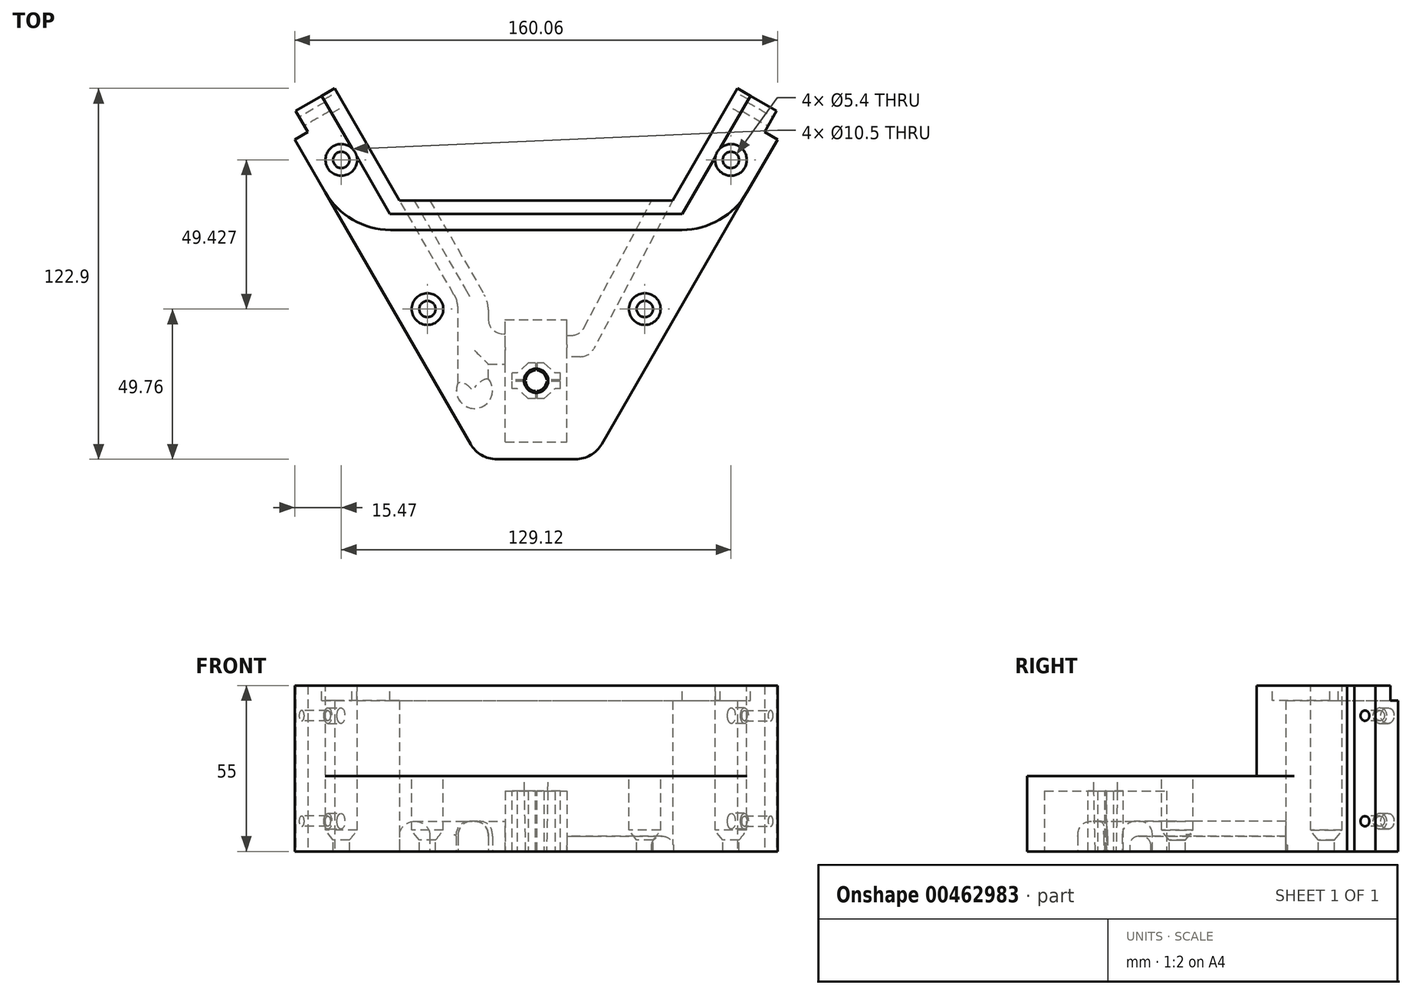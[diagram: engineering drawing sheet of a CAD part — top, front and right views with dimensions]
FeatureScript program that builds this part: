
annotation { "Feature Type Name" : "Feature", "Feature Type Description" : "" }
export const myFeature = defineFeature(function(context is Context, id is Id, definition is map)
    precondition{}
    {
        {
            var Q0;
            Q0=qCreatedBy(makeId("Top.planeOp"),FACE);
            var sketch = newSketch(context, id + "F0", { "sketchPlane" : qUnion([Q0])});
            skLineSegment(sketch, "E0.bottom", {"start": v(53.2, 49.76) * mm, "end": v(-53.2, 49.76) * mm, "construction": true});
            skLineSegment(sketch, "E0.top", {"start": v(53.2, -49.76) * mm, "end": v(-53.2, -49.76) * mm, "construction": true});
            skLineSegment(sketch, "E0.left", {"start": v(53.2, 49.76) * mm, "end": v(53.2, -49.76) * mm, "construction": true});
            skLineSegment(sketch, "E0.right", {"start": v(-53.2, 49.76) * mm, "end": v(-53.2, -49.76) * mm, "construction": true});
            skPoint(sketch, "E0.middle", {"position": v(0, 0) * mm});
            skLineSegment(sketch, "E1", {"start": v(-53.2, 49.76) * mm, "end": v(-48, 52.76) * mm, "construction": true});
            skLineSegment(sketch, "E2", {"start": v(-48, 52.76) * mm, "end": v(-40.64, 40) * mm, "construction": true});
            skLineSegment(sketch, "E3", {"start": v(53.2, 49.76) * mm, "end": v(48, 52.76) * mm, "construction": true});
            skLineSegment(sketch, "E4", {"start": v(48, 52.76) * mm, "end": v(40.64, 40) * mm, "construction": true});
            skLineSegment(sketch, "E5", {"start": v(16.54, -13.75) * mm, "end": v(33.86, -23.75) * mm, "construction": true});
            skLineSegment(sketch, "E6", {"start": v(80.03, 56.21) * mm, "end": v(21.73, -44.76) * mm});
            skLineSegment(sketch, "E7", {"start": v(-16.53, -13.75) * mm, "end": v(-33.86, -23.75) * mm, "construction": true});
            skLineSegment(sketch, "E8", {"start": v(-80.03, 56.21) * mm, "end": v(-21.73, -44.76) * mm});
            skLineSegment(sketch, "E9", {"start": v(-13.07, -49.76) * mm, "end": v(13.07, -49.76) * mm});
            skPoint(sketch, "E10.visualSharp", {"position": v(-18.84, -49.76) * mm});
            skArc(sketch, "E10.filletArc", {"start": v(-21.73, -44.76) * mm, "mid": v(-18.07, -48.42) * mm, "end": v(-13.07, -49.76) * mm});
            skPoint(sketch, "E11.visualSharp", {"position": v(18.84, -49.76) * mm});
            skArc(sketch, "E11.filletArc", {"start": v(13.07, -49.76) * mm, "mid": v(18.07, -48.42) * mm, "end": v(21.73, -44.76) * mm});
            skLineSegment(sketch, "E12.bottom", {"start": v(10, -43.76) * mm, "end": v(-10, -43.76) * mm, "construction": true});
            skLineSegment(sketch, "E12.top", {"start": v(10, -3.76) * mm, "end": v(-10, -3.76) * mm, "construction": true});
            skLineSegment(sketch, "E12.left", {"start": v(10, -43.76) * mm, "end": v(10, -3.76) * mm, "construction": true});
            skLineSegment(sketch, "E12.right", {"start": v(-10, -43.76) * mm, "end": v(-10, -3.76) * mm, "construction": true});
            skPoint(sketch, "E12.middle", {"position": v(0, -23.76) * mm});
            skLineSegment(sketch, "E13", {"start": v(14.22, 4.24) * mm, "end": v(-14.22, 4.24) * mm, "construction": true});
            skPoint(sketch, "E14.orphan", {"position": v(-19.1, 2.67) * mm});
            skPoint(sketch, "E15.orphan", {"position": v(19.1, 2.67) * mm});
            skPoint(sketch, "E16.visualSharp", {"position": v(-20, 4.24) * mm});
            skArc(sketch, "E16.filletArc", {"start": v(-22.88, 9.24) * mm, "mid": v(-19.22, 5.58) * mm, "end": v(-14.22, 4.24) * mm, "construction": true});
            skPoint(sketch, "E17.visualSharp", {"position": v(20, 4.24) * mm});
            skArc(sketch, "E17.filletArc", {"start": v(14.22, 4.24) * mm, "mid": v(19.22, 5.58) * mm, "end": v(22.88, 9.24) * mm, "construction": true});
            skLineSegment(sketch, "E18", {"start": v(32.55, 32) * mm, "end": v(-32.55, 31.99) * mm, "construction": true});
            skLineSegment(sketch, "E19", {"start": v(-45.25, 35.99) * mm, "end": v(45.25, 36) * mm});
            skLineSegment(sketch, "E20.trimOffspring", {"start": v(-34.29, 29) * mm, "end": v(-22.88, 9.24) * mm, "construction": true});
            skLineSegment(sketch, "E21.trimOffspring", {"start": v(34.29, 29) * mm, "end": v(22.88, 9.24) * mm, "construction": true});
            skPoint(sketch, "E22.visualSharp", {"position": v(-36.02, 31.99) * mm});
            skArc(sketch, "E22.filletArc", {"start": v(-32.55, 31.99) * mm, "mid": v(-34.29, 30.99) * mm, "end": v(-34.29, 28.99) * mm, "construction": true});
            skPoint(sketch, "E23.visualSharp", {"position": v(36.02, 32) * mm});
            skArc(sketch, "E23.filletArc", {"start": v(34.29, 29) * mm, "mid": v(34.29, 31) * mm, "end": v(32.55, 32) * mm, "construction": true});
            skPoint(sketch, "E24.visualSharp", {"position": v(-38.33, 36) * mm});
            skArc(sketch, "E24.filletArc", {"start": v(-40.64, 39.99) * mm, "mid": v(-37.7, 37.06) * mm, "end": v(-33.7, 36) * mm, "construction": true});
            skPoint(sketch, "E25.visualSharp", {"position": v(38.33, 36) * mm});
            skArc(sketch, "E25.filletArc", {"start": v(33.7, 36) * mm, "mid": v(37.7, 37.06) * mm, "end": v(40.64, 40) * mm, "construction": true});
            skLineSegment(sketch, "E26", {"start": v(-53.2, 29.76) * mm, "end": v(-15.63, -35.33) * mm, "construction": true});
            skLineSegment(sketch, "E27", {"start": v(53.2, 29.76) * mm, "end": v(15.63, -35.33) * mm, "construction": true});
            skCircle(sketch, "E28", {"center": v(-20.45, -26.98) * mm, "radius": 6 * mm, "construction": true});
            skCircle(sketch, "E29", {"center": v(20.45, -26.98) * mm, "radius": 6 * mm, "construction": true});
            skLineSegment(sketch, "E30", {"start": v(-45.25, 35.99) * mm, "end": v(-66.7, 73.14) * mm});
            skLineSegment(sketch, "E31", {"start": v(-66.7, 73.14) * mm, "end": v(-79.7, 65.64) * mm});
            skLineSegment(sketch, "E32", {"start": v(45.25, 36) * mm, "end": v(66.7, 73.14) * mm});
            skLineSegment(sketch, "E33", {"start": v(66.7, 73.14) * mm, "end": v(79.7, 65.64) * mm});
            skLineSegment(sketch, "E34", {"start": v(-45.25, 35.99) * mm, "end": v(-16.53, -13.75) * mm, "construction": true});
            skLineSegment(sketch, "E35", {"start": v(45.25, 36) * mm, "end": v(45.25, 36) * mm});
            skLineSegment(sketch, "E36", {"start": v(45.25, 36) * mm, "end": v(16.54, -13.75) * mm, "construction": true});
            skLineSegment(sketch, "E37", {"start": v(-79.7, 65.64) * mm, "end": v(-75.7, 58.71) * mm});
            skLineSegment(sketch, "E38", {"start": v(-75.7, 58.71) * mm, "end": v(-80.03, 56.21) * mm});
            skLineSegment(sketch, "E39", {"start": v(79.7, 65.64) * mm, "end": v(75.7, 58.71) * mm});
            skLineSegment(sketch, "E40", {"start": v(75.7, 58.71) * mm, "end": v(80.03, 56.21) * mm});
            skSolve(sketch);
        }
        {
            var Q0;
            Q0 = qSketchRegion(id + "F0", true);
            extrude(context, id + "F1", {"entities" : qUnion([Q0]), "depth" : 25 * mm, "offsetDistance" : 25 * mm});
        }
        {
            var Q0;
            Q0=makeQuery(id+"F0.imprint","IMPRINT",FACE,{"disambiguationData":[TD([[makeQuery(id+"F0.imprint","IMPRINT",EDGE,{"derivedFrom":sQuery(id+"F0.wireOp",EDGE,"E6")}),-1.0]])]});
            var sketch = newSketch(context, id + "F2", { "sketchPlane" : qUnion([Q0])});
            skLineSegment(sketch, "E41.bottom", {"start": v(10, -43.74) * mm, "end": v(-10, -43.74) * mm});
            skLineSegment(sketch, "E41.top", {"start": v(10, -3.74) * mm, "end": v(-10, -3.74) * mm});
            skLineSegment(sketch, "E41.left", {"start": v(10, -43.74) * mm, "end": v(10, -3.74) * mm});
            skLineSegment(sketch, "E41.right", {"start": v(-10, -43.74) * mm, "end": v(-10, -18.24) * mm});
            skPoint(sketch, "E41.middle", {"position": v(0, -23.74) * mm});
            skArc(sketch, "E42", {"start": v(-25.87, -24.4) * mm, "mid": v(-19.66, -32.9) * mm, "end": v(-15.87, -23.08) * mm});
            skLineSegment(sketch, "E43", {"start": v(-25.87, -24.4) * mm, "end": v(-25.87, -0.24) * mm});
            skLineSegment(sketch, "E44", {"start": v(-27.21, 4.76) * mm, "end": v(-45.25, 36) * mm});
            skLineSegment(sketch, "E45", {"start": v(-45.25, 36) * mm, "end": v(-35.25, 36) * mm});
            skLineSegment(sketch, "E46", {"start": v(-35.25, 36) * mm, "end": v(-17.21, 4.76) * mm});
            skPoint(sketch, "E47.visualSharp", {"position": v(-25.87, 2.44) * mm});
            skArc(sketch, "E47.filletArc", {"start": v(-25.87, -0.24) * mm, "mid": v(-26.21, 2.35) * mm, "end": v(-27.21, 4.76) * mm});
            skPoint(sketch, "E48.visualSharp", {"position": v(-15.87, 2.44) * mm});
            skArc(sketch, "E48.filletArc", {"start": v(-15.87, -0.24) * mm, "mid": v(-16.21, 2.35) * mm, "end": v(-17.21, 4.76) * mm});
            skLineSegment(sketch, "E49", {"start": v(-15.87, -23.08) * mm, "end": v(-15.87, -18.24) * mm});
            skLineSegment(sketch, "E50", {"start": v(-15.87, -18.24) * mm, "end": v(-10, -18.24) * mm});
            skLineSegment(sketch, "E51", {"start": v(-10.87, -8.24) * mm, "end": v(-10, -8.24) * mm});
            skLineSegment(sketch, "E52", {"start": v(-15.87, -0.24) * mm, "end": v(-15.87, -3.24) * mm});
            skPoint(sketch, "E53.visualSharp", {"position": v(-15.87, -8.24) * mm});
            skArc(sketch, "E53.filletArc", {"start": v(-15.87, -3.24) * mm, "mid": v(-14.4, -6.77) * mm, "end": v(-10.87, -8.24) * mm});
            skLineSegment(sketch, "E54.trimOffspring", {"start": v(-10, -8.24) * mm, "end": v(-10, -3.74) * mm});
            skSolve(sketch);
        }
        {
            var Q0;
            Q0 = qSketchRegion(id + "F2", true);
            extrude(context, id + "F3", {"entities" : qUnion([Q0]), "operationType" : NewBodyOperationType.REMOVE, "depth" : 10 * mm, "offsetDistance" : 25 * mm});
        }
        {
            var Q0;
            Q0=makeQuery(id+"F3.boolean.opBoolean","COPY",EDGE,{"derivedFrom":makeQuery(id+"F3.opExtrude","CAP_EDGE",EDGE,{"disambiguationData":[OSD([sQuery(id+"F2.wireOp",EDGE,"E44")])],"isStart":false})});
            var Q1;
            Q1=makeQuery(id+"F3.boolean.opBoolean","COPY",EDGE,{"derivedFrom":makeQuery(id+"F3.opExtrude","CAP_EDGE",EDGE,{"disambiguationData":[OSD([sQuery(id+"F2.wireOp",EDGE,"E46")])],"isStart":false})});
            var Q2;
            Q2=makeQuery(id+"F3.boolean.opBoolean","COPY",EDGE,{"derivedFrom":makeQuery(id+"F3.opExtrude","CAP_EDGE",EDGE,{"disambiguationData":[OSD([sQuery(id+"F2.wireOp",EDGE,"E50")])],"isStart":false})});
            var Q3;
            Q3=makeQuery(id+"F3.boolean.opBoolean","COPY",EDGE,{"derivedFrom":makeQuery(id+"F3.opExtrude","CAP_EDGE",EDGE,{"disambiguationData":[OSD([sQuery(id+"F2.wireOp",EDGE,"E49")])],"isStart":false})});
            fillet(context, id + "F4", {"entities" : qUnion([Q0, Q1, Q2, Q3]), "radius" : 4.5 * mm, "tangentPropagation" : true, "allowEdgeOverflow" : false});
        }
        {
            var Q0;
            Q0=makeQuery(id+"F3.boolean.opBoolean","COPY",EDGE,{"derivedFrom":makeQuery(id+"F3.opExtrude","CAP_EDGE",EDGE,{"disambiguationData":[OSD([sQuery(id+"F2.wireOp",EDGE,"E42")])],"isStart":false})});
            fillet(context, id + "F5", {"entities" : qUnion([Q0]), "radius" : 5 * mm, "rho" : 0.5, "crossSection" : FilletCrossSection.CONIC, "allowEdgeOverflow" : false});
        }
        {
            var Q0;
            Q0=makeQuery(id+"F0.imprint","IMPRINT",FACE,{"disambiguationData":[TD([[makeQuery(id+"F0.imprint","IMPRINT",EDGE,{"derivedFrom":sQuery(id+"F0.wireOp",EDGE,"E6")}),-1.0]])]});
            var sketch = newSketch(context, id + "F6", { "sketchPlane" : qUnion([Q0])});
            skLineSegment(sketch, "E55", {"start": v(9.52, -8.78) * mm, "end": v(11.51, -8.78) * mm});
            skLineSegment(sketch, "E56", {"start": v(15.93, -6.12) * mm, "end": v(39.82, 38.9) * mm});
            skLineSegment(sketch, "E57", {"start": v(39.82, 38.9) * mm, "end": v(46.82, 38.9) * mm});
            skLineSegment(sketch, "E58", {"start": v(46.82, 38.9) * mm, "end": v(19.1, -13.15) * mm});
            skLineSegment(sketch, "E59", {"start": v(14.7, -15.8) * mm, "end": v(9.5, -15.8) * mm});
            skLineSegment(sketch, "E60", {"start": v(9.5, -15.8) * mm, "end": v(9.52, -8.78) * mm});
            skPoint(sketch, "E61.visualSharp", {"position": v(14.52, -8.78) * mm});
            skArc(sketch, "E61.filletArc", {"start": v(11.51, -8.78) * mm, "mid": v(14.09, -8.06) * mm, "end": v(15.93, -6.12) * mm});
            skPoint(sketch, "E62.visualSharp", {"position": v(17.7, -15.8) * mm});
            skArc(sketch, "E62.filletArc", {"start": v(14.7, -15.8) * mm, "mid": v(17.27, -15.09) * mm, "end": v(19.1, -13.15) * mm});
            skSolve(sketch);
        }
        {
            var Q0;
            Q0 = qSketchRegion(id + "F6", true);
            extrude(context, id + "F7", {"entities" : qUnion([Q0]), "operationType" : NewBodyOperationType.REMOVE, "depth" : 5 * mm, "offsetDistance" : 25 * mm});
        }
        {
            var Q0;
            Q0=makeQuery(id+"F7.boolean.opBoolean","COPY",EDGE,{"derivedFrom":makeQuery(id+"F7.opExtrude","CAP_EDGE",EDGE,{"disambiguationData":[OSD([sQuery(id+"F6.wireOp",EDGE,"E58")])],"isStart":false})});
            var Q1;
            Q1=makeQuery(id+"F7.boolean.opBoolean","COPY",EDGE,{"derivedFrom":makeQuery(id+"F7.opExtrude","CAP_EDGE",EDGE,{"disambiguationData":[OSD([sQuery(id+"F6.wireOp",EDGE,"E56")])],"isStart":false})});
            fillet(context, id + "F8", {"entities" : qUnion([Q0, Q1]), "radius" : 3 * mm, "tangentPropagation" : true, "allowEdgeOverflow" : false});
        }
        {
            var Q0;
            Q0=makeQuery(id+"F0.imprint","IMPRINT",FACE,{"disambiguationData":[TD([[makeQuery(id+"F0.imprint","IMPRINT",EDGE,{"derivedFrom":sQuery(id+"F0.wireOp",EDGE,"E6")}),-1.0]])]});
            var sketch = newSketch(context, id + "F9", { "sketchPlane" : qUnion([Q0])});
            skLineSegment(sketch, "E63.bottom", {"start": v(-10.25, -44) * mm, "end": v(10.25, -44) * mm});
            skLineSegment(sketch, "E63.top", {"start": v(-10.25, -3.5) * mm, "end": v(10.25, -3.5) * mm});
            skLineSegment(sketch, "E63.left", {"start": v(-10.25, -44) * mm, "end": v(-10.25, -3.5) * mm});
            skLineSegment(sketch, "E63.right", {"start": v(10.25, -44) * mm, "end": v(10.25, -3.5) * mm});
            skSolve(sketch);
        }
        {
            var Q0;
            Q0 = qSketchRegion(id + "F9", true);
            extrude(context, id + "F10", {"entities" : qUnion([Q0]), "operationType" : NewBodyOperationType.REMOVE, "depth" : 20 * mm, "offsetDistance" : 25 * mm});
        }
        {
            var Q0;
            Q0=makeQuery(id+"F0.imprint","IMPRINT",FACE,{"disambiguationData":[TD([[makeQuery(id+"F0.imprint","IMPRINT",EDGE,{"derivedFrom":sQuery(id+"F0.wireOp",EDGE,"E6")}),-1.0]])]});
            var sketch = newSketch(context, id + "F11", { "sketchPlane" : qUnion([Q0])});
            skLineSegment(sketch, "E64.bottom", {"start": v(2.6, -17.89) * mm, "end": v(-2.6, -17.89) * mm, "construction": true});
            skLineSegment(sketch, "E64.top", {"start": v(2.6, -29.64) * mm, "end": v(-2.6, -29.64) * mm, "construction": true});
            skLineSegment(sketch, "E64.left", {"start": v(8, -21.16) * mm, "end": v(8, -26.36) * mm, "construction": true});
            skLineSegment(sketch, "E64.right", {"start": v(-8, -21.16) * mm, "end": v(-8, -26.36) * mm, "construction": true});
            skPoint(sketch, "E64.middle", {"position": v(0, -23.76) * mm});
            skLineSegment(sketch, "E65.bottom", {"start": v(8, -26.36) * mm, "end": v(6.25, -26.36) * mm});
            skLineSegment(sketch, "E65.top", {"start": v(8, -21.16) * mm, "end": v(6.25, -21.16) * mm});
            skLineSegment(sketch, "E65.left", {"start": v(8, -26.36) * mm, "end": v(8, -21.16) * mm});
            skLineSegment(sketch, "E65.right", {"start": v(-8, -26.36) * mm, "end": v(-8, -21.16) * mm});
            skLineSegment(sketch, "E66.bottom", {"start": v(2.6, -29.64) * mm, "end": v(-2.6, -29.64) * mm});
            skLineSegment(sketch, "E66.top", {"start": v(2.6, -17.89) * mm, "end": v(-2.6, -17.89) * mm});
            skLineSegment(sketch, "E66.left", {"start": v(2.6, -29.64) * mm, "end": v(2.6, -17.89) * mm, "construction": true});
            skLineSegment(sketch, "E66.right", {"start": v(-2.6, -29.64) * mm, "end": v(-2.6, -17.89) * mm, "construction": true});
            skPoint(sketch, "E67.orphan", {"position": v(-8, -17.89) * mm});
            skPoint(sketch, "E68.orphan", {"position": v(-8, -29.64) * mm});
            skPoint(sketch, "E69.orphan", {"position": v(8, -29.64) * mm});
            skPoint(sketch, "E70.orphan", {"position": v(8, -17.89) * mm});
            skLineSegment(sketch, "E71", {"start": v(-6.25, -26.36) * mm, "end": v(-6.25, -21.16) * mm, "construction": true});
            skLineSegment(sketch, "E72", {"start": v(6.25, -26.36) * mm, "end": v(6.25, -21.16) * mm, "construction": true});
            skLineSegment(sketch, "E73", {"start": v(-2.6, -29.64) * mm, "end": v(-6.25, -26.36) * mm});
            skLineSegment(sketch, "E74", {"start": v(2.6, -29.64) * mm, "end": v(6.25, -26.36) * mm});
            skLineSegment(sketch, "E75", {"start": v(2.6, -17.89) * mm, "end": v(6.25, -21.16) * mm});
            skLineSegment(sketch, "E76", {"start": v(-2.6, -17.89) * mm, "end": v(-6.25, -21.16) * mm});
            skLineSegment(sketch, "E77", {"start": v(-6.25, -26.36) * mm, "end": v(-8, -26.36) * mm});
            skLineSegment(sketch, "E78", {"start": v(6.25, -26.36) * mm, "end": v(-6.25, -26.36) * mm, "construction": true});
            skLineSegment(sketch, "E79", {"start": v(6.25, -21.16) * mm, "end": v(-6.25, -21.16) * mm, "construction": true});
            skLineSegment(sketch, "E80", {"start": v(-6.25, -21.16) * mm, "end": v(-8, -21.16) * mm});
            skSolve(sketch);
        }
        {
            var Q0;
            Q0 = qSketchRegion(id + "F11", true);
            extrude(context, id + "F12", {"entities" : qUnion([Q0]), "operationType" : NewBodyOperationType.ADD, "depth" : 20 * mm, "offsetDistance" : 25 * mm});
        }
        {
            var Q0;
            Q0=makeQuery(id+"F1.opExtrude","CAP_FACE",FACE,{"disambiguationData":[OSD([sQuery(id+"F0.wireOp",EDGE,"E6"),sQuery(id+"F0.wireOp",EDGE,"E8"),sQuery(id+"F0.wireOp",EDGE,"E9"),sQuery(id+"F0.wireOp",EDGE,"E10.filletArc"),sQuery(id+"F0.wireOp",EDGE,"E11.filletArc"),sQuery(id+"F0.wireOp",EDGE,"E19"),sQuery(id+"F0.wireOp",EDGE,"E30"),sQuery(id+"F0.wireOp",EDGE,"E31"),sQuery(id+"F0.wireOp",EDGE,"E32"),sQuery(id+"F0.wireOp",EDGE,"E33")])],"isStart":false});
            var sketch = newSketch(context, id + "F13", { "sketchPlane" : qUnion([Q0])});
            skCircle(sketch, "E81", {"center": v(0, -23.76) * mm, "radius": 4 * mm});
            skSolve(sketch);
        }
        {
            var Q0;
            Q0 = qSketchRegion(id + "F13", true);
            extrude(context, id + "F14", {"entities" : qUnion([Q0]), "operationType" : NewBodyOperationType.REMOVE, "oppositeDirection" : true, "depth" : 25 * mm, "offsetDistance" : 25 * mm, "hasDraft" : true, "draftAngle" : 1.25 * degree, "draftPullDirection" : true});
        }
        {
            var Q0;
            Q0=makeQuery(id+"F0.imprint","IMPRINT",FACE,{"disambiguationData":[TD([[makeQuery(id+"F0.imprint","IMPRINT",EDGE,{"derivedFrom":sQuery(id+"F0.wireOp",EDGE,"E6")}),-1.0]])]});
            var sketch = newSketch(context, id + "F15", { "sketchPlane" : qUnion([Q0])});
            skLineSegment(sketch, "E82.bottom", {"start": v(8.1, -23.51) * mm, "end": v(0.25, -23.51) * mm});
            skLineSegment(sketch, "E82.top", {"start": v(8.1, -24.01) * mm, "end": v(0.25, -24.01) * mm});
            skLineSegment(sketch, "E82.left", {"start": v(8.1, -23.51) * mm, "end": v(8.1, -24.01) * mm});
            skLineSegment(sketch, "E82.right", {"start": v(-8.1, -23.51) * mm, "end": v(-8.1, -24.01) * mm});
            skPoint(sketch, "E82.middle", {"position": v(0, -23.76) * mm});
            skLineSegment(sketch, "E83.bottom", {"start": v(0.25, -17.76) * mm, "end": v(-0.25, -17.76) * mm});
            skLineSegment(sketch, "E83.top", {"start": v(0.25, -29.76) * mm, "end": v(-0.25, -29.76) * mm});
            skLineSegment(sketch, "E83.left", {"start": v(0.25, -17.76) * mm, "end": v(0.25, -23.51) * mm});
            skLineSegment(sketch, "E83.right", {"start": v(-0.25, -17.76) * mm, "end": v(-0.25, -23.51) * mm});
            skLineSegment(sketch, "E84.trimOffspring", {"start": v(-0.25, -24.01) * mm, "end": v(-0.25, -29.76) * mm});
            skLineSegment(sketch, "E85.trimOffspring", {"start": v(-0.25, -24.01) * mm, "end": v(-8.1, -24.01) * mm});
            skLineSegment(sketch, "E86.trimOffspring", {"start": v(0.25, -24.01) * mm, "end": v(0.25, -29.76) * mm});
            skLineSegment(sketch, "E87.trimOffspring", {"start": v(-0.25, -23.51) * mm, "end": v(-8.1, -23.51) * mm});
            skSolve(sketch);
        }
        {
            var Q0;
            Q0 = qSketchRegion(id + "F15", true);
            extrude(context, id + "F16", {"entities" : qUnion([Q0]), "operationType" : NewBodyOperationType.REMOVE, "depth" : 20 * mm, "offsetDistance" : 25 * mm});
        }
        {
            var Q0;
            Q0=makeQuery(id+"F1.opExtrude","CAP_FACE",FACE,{"disambiguationData":[OSD([sQuery(id+"F0.wireOp",EDGE,"E6"),sQuery(id+"F0.wireOp",EDGE,"E8"),sQuery(id+"F0.wireOp",EDGE,"E9"),sQuery(id+"F0.wireOp",EDGE,"E10.filletArc"),sQuery(id+"F0.wireOp",EDGE,"E11.filletArc"),sQuery(id+"F0.wireOp",EDGE,"E19"),sQuery(id+"F0.wireOp",EDGE,"E30"),sQuery(id+"F0.wireOp",EDGE,"E31"),sQuery(id+"F0.wireOp",EDGE,"E32"),sQuery(id+"F0.wireOp",EDGE,"E33")])],"isStart":false});
            var sketch = newSketch(context, id + "F17", { "sketchPlane" : qUnion([Q0])});
            skLineSegment(sketch, "E88", {"start": v(-45.25, 35.99) * mm, "end": v(-66.7, 73.14) * mm});
            skLineSegment(sketch, "E89", {"start": v(-66.7, 73.14) * mm, "end": v(-79.7, 65.64) * mm});
            skLineSegment(sketch, "E90", {"start": v(-80.03, 56.21) * mm, "end": v(-69.94, 38.74) * mm});
            skLineSegment(sketch, "E91", {"start": v(-48.29, 26.24) * mm, "end": v(48.29, 26.24) * mm});
            skLineSegment(sketch, "E92", {"start": v(69.94, 38.74) * mm, "end": v(80.03, 56.21) * mm});
            skLineSegment(sketch, "E93", {"start": v(79.7, 65.64) * mm, "end": v(66.7, 73.14) * mm});
            skLineSegment(sketch, "E94", {"start": v(66.7, 73.14) * mm, "end": v(45.25, 36) * mm});
            skLineSegment(sketch, "E95", {"start": v(45.25, 36) * mm, "end": v(-45.25, 35.99) * mm});
            skPoint(sketch, "E96.visualSharp", {"position": v(-62.72, 26.24) * mm});
            skArc(sketch, "E96.filletArc", {"start": v(-69.94, 38.74) * mm, "mid": v(-60.79, 29.59) * mm, "end": v(-48.29, 26.24) * mm});
            skPoint(sketch, "E97.visualSharp", {"position": v(62.72, 26.24) * mm});
            skArc(sketch, "E97.filletArc", {"start": v(48.29, 26.24) * mm, "mid": v(60.79, 29.59) * mm, "end": v(69.94, 38.74) * mm});
            skLineSegment(sketch, "E98", {"start": v(-79.7, 65.64) * mm, "end": v(-75.7, 58.71) * mm});
            skLineSegment(sketch, "E99", {"start": v(-75.7, 58.71) * mm, "end": v(-80.03, 56.21) * mm});
            skLineSegment(sketch, "E100", {"start": v(79.7, 65.64) * mm, "end": v(75.7, 58.71) * mm});
            skLineSegment(sketch, "E101", {"start": v(75.7, 58.71) * mm, "end": v(80.03, 56.21) * mm});
            skSolve(sketch);
        }
        {
            var Q0;
            Q0 = qSketchRegion(id + "F17", true);
            extrude(context, id + "F18", {"entities" : qUnion([Q0]), "operationType" : NewBodyOperationType.ADD, "depth" : 30 * mm, "offsetDistance" : 25 * mm});
        }
        {
            var Q0;
            Q0=makeQuery(id+"F18.opExtrude","CAP_FACE",FACE,{"disambiguationData":[OSD([sQuery(id+"F17.wireOp",EDGE,"E88"),sQuery(id+"F17.wireOp",EDGE,"E89"),sQuery(id+"F17.wireOp",EDGE,"E90"),sQuery(id+"F17.wireOp",EDGE,"E91"),sQuery(id+"F17.wireOp",EDGE,"E92"),sQuery(id+"F17.wireOp",EDGE,"E93"),sQuery(id+"F17.wireOp",EDGE,"E94"),sQuery(id+"F17.wireOp",EDGE,"E95"),sQuery(id+"F17.wireOp",EDGE,"E96.filletArc"),sQuery(id+"F17.wireOp",EDGE,"E97.filletArc")])],"isStart":false});
            var sketch = newSketch(context, id + "F19", { "sketchPlane" : qUnion([Q0])});
            skLineSegment(sketch, "E102", {"start": v(-45.25, 35.99) * mm, "end": v(-66.7, 73.14) * mm});
            skLineSegment(sketch, "E103", {"start": v(-66.7, 73.14) * mm, "end": v(-71.04, 70.64) * mm});
            skLineSegment(sketch, "E104", {"start": v(-71.04, 70.64) * mm, "end": v(-48.44, 31.5) * mm});
            skLineSegment(sketch, "E105", {"start": v(-48.44, 31.5) * mm, "end": v(48.44, 31.5) * mm});
            skLineSegment(sketch, "E106", {"start": v(48.44, 31.5) * mm, "end": v(71.04, 70.64) * mm});
            skLineSegment(sketch, "E107", {"start": v(71.04, 70.64) * mm, "end": v(66.7, 73.14) * mm});
            skLineSegment(sketch, "E108", {"start": v(66.7, 73.14) * mm, "end": v(45.25, 36) * mm});
            skLineSegment(sketch, "E109", {"start": v(45.25, 36) * mm, "end": v(-45.25, 35.99) * mm});
            skSolve(sketch);
        }
        {
            var Q0;
            Q0 = qSketchRegion(id + "F19", true);
            extrude(context, id + "F20", {"entities" : qUnion([Q0]), "operationType" : NewBodyOperationType.REMOVE, "oppositeDirection" : true, "depth" : 5 * mm, "offsetDistance" : 25 * mm});
        }
        {
            var Q0;
            Q0=makeQuery(id+"F18.opExtrude","CAP_FACE",FACE,{"disambiguationData":[OSD([sQuery(id+"F17.wireOp",EDGE,"E88"),sQuery(id+"F17.wireOp",EDGE,"E89"),sQuery(id+"F17.wireOp",EDGE,"E90"),sQuery(id+"F17.wireOp",EDGE,"E91"),sQuery(id+"F17.wireOp",EDGE,"E92"),sQuery(id+"F17.wireOp",EDGE,"E93"),sQuery(id+"F17.wireOp",EDGE,"E94"),sQuery(id+"F17.wireOp",EDGE,"E95"),sQuery(id+"F17.wireOp",EDGE,"E96.filletArc"),sQuery(id+"F17.wireOp",EDGE,"E97.filletArc")])],"isStart":false});
            var sketch = newSketch(context, id + "F21", { "sketchPlane" : qUnion([Q0])});
            skLineSegment(sketch, "E110", {"start": v(-75.37, 68.14) * mm, "end": v(-53.4, 30.1) * mm, "construction": true});
            skLineSegment(sketch, "E111", {"start": v(75.37, 68.14) * mm, "end": v(55.87, 34.37) * mm, "construction": true});
            skLineSegment(sketch, "E112", {"start": v(-89.25, 49.43) * mm, "end": v(82.56, 49.43) * mm, "construction": true});
            skCircle(sketch, "E113", {"center": v(-64.56, 49.43) * mm, "radius": 5.25 * mm});
            skCircle(sketch, "E114", {"center": v(64.56, 49.43) * mm, "radius": 5.25 * mm});
            skSolve(sketch);
        }
        {
            var Q0;
            Q0 = qSketchRegion(id + "F21", true);
            extrude(context, id + "F22", {"entities" : qUnion([Q0]), "operationType" : NewBodyOperationType.REMOVE, "oppositeDirection" : true, "depth" : 48 * mm, "offsetDistance" : 25 * mm});
        }
        {
            var Q0;
            Q0=makeQuery(id+"F22.boolean.opBoolean","COPY",FACE,{"derivedFrom":makeQuery(id+"F22.opExtrude","CAP_FACE",FACE,{"disambiguationData":[OSD([sQuery(id+"F21.wireOp",EDGE,"E113")])],"isStart":false})});
            var sketch = newSketch(context, id + "F23", { "sketchPlane" : qUnion([Q0])});
            skCircle(sketch, "E115", {"center": v(-64.56, 49.43) * mm, "radius": 5.25 * mm});
            skSolve(sketch);
        }
        {
            var Q0;
            Q0=makeQuery(id+"F22.boolean.opBoolean","COPY",FACE,{"derivedFrom":makeQuery(id+"F22.opExtrude","CAP_FACE",FACE,{"disambiguationData":[OSD([sQuery(id+"F21.wireOp",EDGE,"E114")])],"isStart":false})});
            var sketch = newSketch(context, id + "F24", { "sketchPlane" : qUnion([Q0])});
            skCircle(sketch, "E116", {"center": v(64.56, 49.43) * mm, "radius": 5.25 * mm});
            skSolve(sketch);
        }
        {
            var Q0;
            Q0 = qSketchRegion(id + "F24", true);
            extrude(context, id + "F25", {"entities" : qUnion([Q0]), "operationType" : NewBodyOperationType.REMOVE, "oppositeDirection" : true, "depth" : 3.3 * mm, "offsetDistance" : 25 * mm, "hasDraft" : true, "draftAngle" : 38 * degree, "draftPullDirection" : true});
        }
        {
            var Q0;
            Q0=makeQuery(id+"F18.opExtrude","CAP_FACE",FACE,{"disambiguationData":[OSD([sQuery(id+"F17.wireOp",EDGE,"E88"),sQuery(id+"F17.wireOp",EDGE,"E89"),sQuery(id+"F17.wireOp",EDGE,"E90"),sQuery(id+"F17.wireOp",EDGE,"E91"),sQuery(id+"F17.wireOp",EDGE,"E92"),sQuery(id+"F17.wireOp",EDGE,"E93"),sQuery(id+"F17.wireOp",EDGE,"E94"),sQuery(id+"F17.wireOp",EDGE,"E95"),sQuery(id+"F17.wireOp",EDGE,"E96.filletArc"),sQuery(id+"F17.wireOp",EDGE,"E97.filletArc")])],"isStart":false});
            var sketch = newSketch(context, id + "F26", { "sketchPlane" : qUnion([Q0])});
            skCircle(sketch, "E117", {"center": v(-64.56, 49.43) * mm, "radius": 2.7 * mm});
            skCircle(sketch, "E118", {"center": v(64.56, 49.43) * mm, "radius": 2.7 * mm});
            skSolve(sketch);
        }
        {
            var Q0;
            Q0 = qSketchRegion(id + "F26", true);
            extrude(context, id + "F27", {"entities" : qUnion([Q0]), "operationType" : NewBodyOperationType.REMOVE, "oppositeDirection" : true, "depth" : 56 * mm, "offsetDistance" : 25 * mm});
        }
        {
            var Q0;
            Q0=makeQuery(id+"F1.opExtrude","CAP_FACE",FACE,{"disambiguationData":[OSD([sQuery(id+"F0.wireOp",EDGE,"E6"),sQuery(id+"F0.wireOp",EDGE,"E8"),sQuery(id+"F0.wireOp",EDGE,"E9"),sQuery(id+"F0.wireOp",EDGE,"E10.filletArc"),sQuery(id+"F0.wireOp",EDGE,"E11.filletArc"),sQuery(id+"F0.wireOp",EDGE,"E19"),sQuery(id+"F0.wireOp",EDGE,"E30"),sQuery(id+"F0.wireOp",EDGE,"E31"),sQuery(id+"F0.wireOp",EDGE,"E32"),sQuery(id+"F0.wireOp",EDGE,"E33")])],"isStart":false});
            var sketch = newSketch(context, id + "F28", { "sketchPlane" : qUnion([Q0])});
            skLineSegment(sketch, "E119", {"start": v(-43.86, 13.57) * mm, "end": v(-26.7, -16.15) * mm, "construction": true});
            skLineSegment(sketch, "E120", {"start": v(42.38, 11) * mm, "end": v(28.2, -13.56) * mm, "construction": true});
            skCircle(sketch, "E121", {"center": v(-36.02, 0) * mm, "radius": 2.7 * mm});
            skCircle(sketch, "E122", {"center": v(36.02, 0) * mm, "radius": 2.7 * mm});
            skSolve(sketch);
        }
        {
            var Q0;
            Q0 = qSketchRegion(id + "F28", true);
            extrude(context, id + "F29", {"entities" : qUnion([Q0]), "operationType" : NewBodyOperationType.REMOVE, "oppositeDirection" : true, "depth" : 25 * mm, "offsetDistance" : 25 * mm});
        }
        {
            var Q0;
            Q0=makeQuery(id+"F1.opExtrude","CAP_FACE",FACE,{"disambiguationData":[OSD([sQuery(id+"F0.wireOp",EDGE,"E6"),sQuery(id+"F0.wireOp",EDGE,"E8"),sQuery(id+"F0.wireOp",EDGE,"E9"),sQuery(id+"F0.wireOp",EDGE,"E10.filletArc"),sQuery(id+"F0.wireOp",EDGE,"E11.filletArc"),sQuery(id+"F0.wireOp",EDGE,"E19"),sQuery(id+"F0.wireOp",EDGE,"E30"),sQuery(id+"F0.wireOp",EDGE,"E31"),sQuery(id+"F0.wireOp",EDGE,"E32"),sQuery(id+"F0.wireOp",EDGE,"E33")])],"isStart":false});
            var sketch = newSketch(context, id + "F30", { "sketchPlane" : qUnion([Q0])});
            skCircle(sketch, "E123", {"center": v(-36.02, 0) * mm, "radius": 5.25 * mm});
            skCircle(sketch, "E124", {"center": v(36.02, 0) * mm, "radius": 5.25 * mm});
            skSolve(sketch);
        }
        {
            var Q0;
            Q0 = qSketchRegion(id + "F30", true);
            extrude(context, id + "F31", {"entities" : qUnion([Q0]), "operationType" : NewBodyOperationType.REMOVE, "oppositeDirection" : true, "depth" : 18 * mm, "offsetDistance" : 25 * mm});
        }
        {
            var Q0;
            Q0=makeQuery(id+"F31.boolean.opBoolean","COPY",FACE,{"derivedFrom":makeQuery(id+"F31.opExtrude","CAP_FACE",FACE,{"disambiguationData":[OSD([sQuery(id+"F30.wireOp",EDGE,"E123")])],"isStart":false})});
            var sketch = newSketch(context, id + "F32", { "sketchPlane" : qUnion([Q0])});
            skCircle(sketch, "E125", {"center": v(-36.02, 0) * mm, "radius": 5.25 * mm});
            skSolve(sketch);
        }
        {
            var Q0;
            Q0 = qSketchRegion(id + "F32", true);
            extrude(context, id + "F33", {"entities" : qUnion([Q0]), "operationType" : NewBodyOperationType.REMOVE, "oppositeDirection" : true, "depth" : 3.3 * mm, "offsetDistance" : 25 * mm, "hasDraft" : true, "draftAngle" : 38 * degree, "draftPullDirection" : true});
        }
        {
            var Q0;
            Q0=makeQuery(id+"F31.boolean.opBoolean","COPY",FACE,{"derivedFrom":makeQuery(id+"F31.opExtrude","CAP_FACE",FACE,{"disambiguationData":[OSD([sQuery(id+"F30.wireOp",EDGE,"E124")])],"isStart":false})});
            var sketch = newSketch(context, id + "F34", { "sketchPlane" : qUnion([Q0])});
            skCircle(sketch, "E126", {"center": v(36.02, 0) * mm, "radius": 5.25 * mm});
            skSolve(sketch);
        }
        {
            var Q0;
            Q0 = qSketchRegion(id + "F34", true);
            extrude(context, id + "F35", {"entities" : qUnion([Q0]), "operationType" : NewBodyOperationType.REMOVE, "oppositeDirection" : true, "depth" : 3.3 * mm, "offsetDistance" : 25 * mm, "hasDraft" : true, "draftAngle" : 38 * degree, "draftPullDirection" : true});
        }
        {
            var Q0;
            Q0=makeQuery(id+"F18.boolean.opBoolean","MERGE",FACE,{"derivedFrom":[makeQuery(id+"F1.opExtrude","SWEPT_FACE",FACE,{"disambiguationData":[OSD([sQuery(id+"F0.wireOp",EDGE,"E37")])]}),makeQuery(id+"F18.opExtrude","SWEPT_FACE",FACE,{"disambiguationData":[OSD([sQuery(id+"F17.wireOp",EDGE,"E98")])]})]});
            var sketch = newSketch(context, id + "F36", { "sketchPlane" : qUnion([Q0])});
            skLineSegment(sketch, "E127", {"start": v(-92.7, 55) * mm, "end": v(-92.7, 0) * mm, "construction": true});
            skCircle(sketch, "E128", {"center": v(-92.7, 45) * mm, "radius": 1.7 * mm});
            skCircle(sketch, "E129", {"center": v(-92.7, 10) * mm, "radius": 1.7 * mm});
            skSolve(sketch);
        }
        {
            var Q0;
            Q0 = qSketchRegion(id + "F36", true);
            extrude(context, id + "F37", {"entities" : qUnion([Q0]), "operationType" : NewBodyOperationType.REMOVE, "oppositeDirection" : true, "depth" : 15 * mm, "offsetDistance" : 25 * mm});
        }
        {
            var Q0;
            Q0=makeQuery(id+"F18.boolean.opBoolean","MERGE",FACE,{"derivedFrom":[makeQuery(id+"F1.opExtrude","SWEPT_FACE",FACE,{"disambiguationData":[OSD([sQuery(id+"F0.wireOp",EDGE,"E39")])]}),makeQuery(id+"F18.opExtrude","SWEPT_FACE",FACE,{"disambiguationData":[OSD([sQuery(id+"F17.wireOp",EDGE,"E100")])]})]});
            var sketch = newSketch(context, id + "F38", { "sketchPlane" : qUnion([Q0])});
            skLineSegment(sketch, "E130", {"start": v(92.7, 55) * mm, "end": v(92.7, 0) * mm, "construction": true});
            skCircle(sketch, "E131", {"center": v(92.7, 45) * mm, "radius": 1.7 * mm});
            skCircle(sketch, "E132", {"center": v(92.7, 10) * mm, "radius": 1.7 * mm});
            skSolve(sketch);
        }
        {
            var Q0;
            Q0 = qSketchRegion(id + "F38", true);
            extrude(context, id + "F39", {"entities" : qUnion([Q0]), "operationType" : NewBodyOperationType.REMOVE, "oppositeDirection" : true, "depth" : 15 * mm, "offsetDistance" : 25 * mm});
        }
        {
            var Q0;
            Q0=makeQuery(id+"F18.boolean.opBoolean","MERGE",FACE,{"derivedFrom":[makeQuery(id+"F1.opExtrude","SWEPT_FACE",FACE,{"disambiguationData":[OSD([sQuery(id+"F0.wireOp",EDGE,"E30")])]}),makeQuery(id+"F18.opExtrude","SWEPT_FACE",FACE,{"disambiguationData":[OSD([sQuery(id+"F17.wireOp",EDGE,"E88")])]})]});
            var sketch = newSketch(context, id + "F40", { "sketchPlane" : qUnion([Q0])});
            skCircle(sketch, "E133", {"center": v(92.7, 10) * mm, "radius": 2.6 * mm});
            skCircle(sketch, "E134", {"center": v(92.7, 45) * mm, "radius": 2.6 * mm});
            skSolve(sketch);
        }
        {
            var Q0;
            Q0 = qSketchRegion(id + "F40", true);
            extrude(context, id + "F41", {"entities" : qUnion([Q0]), "operationType" : NewBodyOperationType.REMOVE, "oppositeDirection" : true, "depth" : 5 * mm, "offsetDistance" : 25 * mm});
        }
        {
            var Q0;
            Q0=makeQuery(id+"F18.boolean.opBoolean","MERGE",FACE,{"derivedFrom":[makeQuery(id+"F1.opExtrude","SWEPT_FACE",FACE,{"disambiguationData":[OSD([sQuery(id+"F0.wireOp",EDGE,"E32")])]}),makeQuery(id+"F18.opExtrude","SWEPT_FACE",FACE,{"disambiguationData":[OSD([sQuery(id+"F17.wireOp",EDGE,"E94")])]})]});
            var sketch = newSketch(context, id + "F42", { "sketchPlane" : qUnion([Q0])});
            skCircle(sketch, "E135", {"center": v(-92.7, 10) * mm, "radius": 2.6 * mm});
            skCircle(sketch, "E136", {"center": v(-92.7, 45) * mm, "radius": 2.6 * mm});
            skSolve(sketch);
        }
        {
            var Q0;
            Q0 = qSketchRegion(id + "F42", true);
            extrude(context, id + "F43", {"entities" : qUnion([Q0]), "operationType" : NewBodyOperationType.REMOVE, "oppositeDirection" : true, "depth" : 5 * mm, "offsetDistance" : 25 * mm});
        }
        {
            var Q0;
            Q0 = qSketchRegion(id + "F23", true);
            extrude(context, id + "F44", {"entities" : qUnion([Q0]), "operationType" : NewBodyOperationType.REMOVE, "oppositeDirection" : true, "depth" : 3.3 * mm, "offsetDistance" : 25 * mm, "hasDraft" : true, "draftAngle" : 38 * degree, "draftPullDirection" : true});
        }
    });
